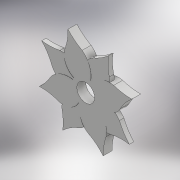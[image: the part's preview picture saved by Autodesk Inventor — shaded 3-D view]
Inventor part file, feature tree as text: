
AUTODESK INVENTOR PART (.ipt)
format: ipt  version: 2017 (Build 210142000, 142)  size: 229,888 bytes
history: native  units: mm
features: extrude x3, sketch x3
ambient origin geometry x8: Origin, YZ Plane, XZ Plane, XY Plane, X Axis, Y Axis, Z Axis, Center Point
bodies: Solid1 (feature_tree)
feature tree (6):
  extrude  "Extrusion1"  Depth=1.0mm TaperAngle=0.0deg
  extrude  "Extrusion2"  Depth=2.0mm TaperAngle=0.0deg
  extrude  "Extrusion3"  [1 undecoded]
  sketch  "Sketch1"  dims[d0=2.0mm d1=0.0mm d2=1.0mm d3=0.0mm]
  sketch  "Sketch2"  dims[d4=4.0mm d5=2.0mm d6=0.0mm]
  sketch  "Sketch3"
note: 1 required parameter value undecoded (feature->parameter linkage not recoverable at this tier; creation-order binding heuristic only, values carry confidence <= 0.55)
